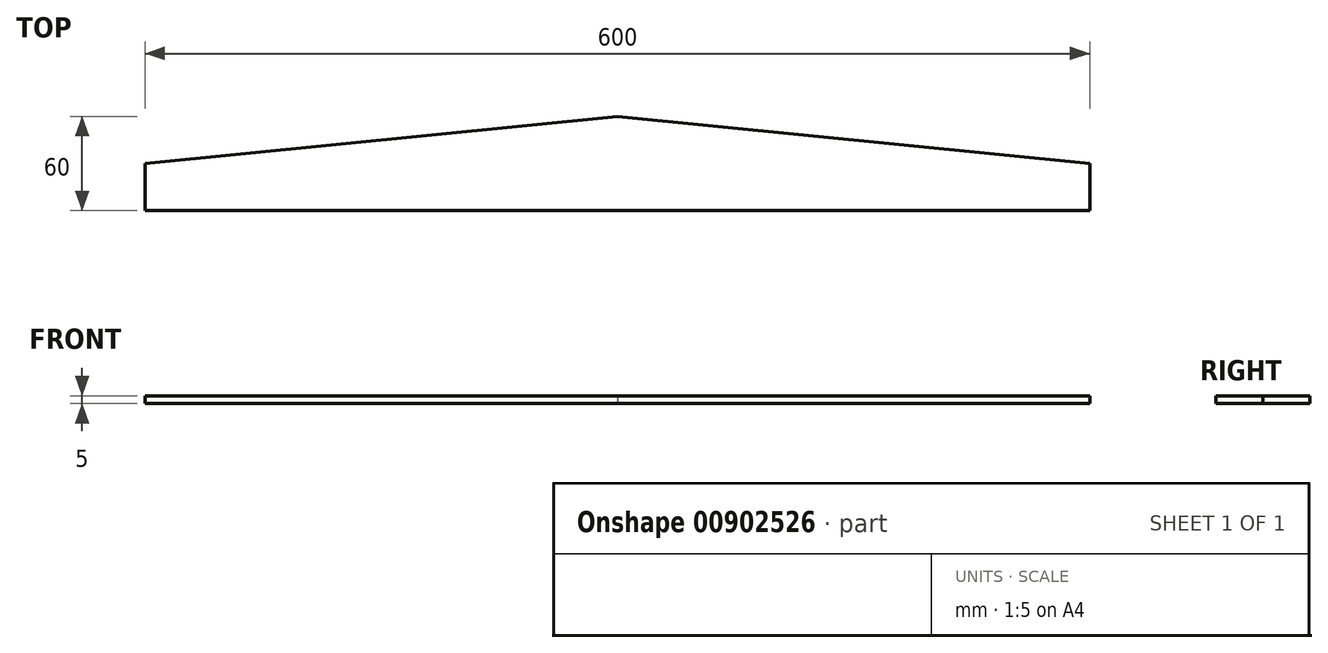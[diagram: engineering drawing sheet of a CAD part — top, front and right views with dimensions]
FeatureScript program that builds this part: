
annotation { "Feature Type Name" : "Feature", "Feature Type Description" : "" }
export const myFeature = defineFeature(function(context is Context, id is Id, definition is map)
    precondition{}
    {
        {
            var Q0;
            Q0=qCreatedBy(makeId("Top.planeOp"),FACE);
            var sketch = newSketch(context, id + "F0", { "sketchPlane" : qUnion([Q0])});
            skLineSegment(sketch, "E0", {"start": v(0, 0) * mm, "end": v(600, 0) * mm});
            skLineSegment(sketch, "E1", {"start": v(300, 0) * mm, "end": v(300, 60) * mm});
            skLineSegment(sketch, "E2", {"start": v(0, 0) * mm, "end": v(0, 30) * mm});
            skLineSegment(sketch, "E3", {"start": v(0, 30) * mm, "end": v(300, 60) * mm});
            skLineSegment(sketch, "E4", {"start": v(600, 0) * mm, "end": v(600, 30) * mm});
            skLineSegment(sketch, "E5", {"start": v(600, 30) * mm, "end": v(300, 60) * mm});
            skSolve(sketch);
        }
        {
            var Q0;
            {var subQ2=sQuery(id+"F0.wireOp",EDGE,"E1");Q0=makeQuery(id+"F0.imprint","IMPRINT",FACE,{"disambiguationData":[TD([[makeQuery(id+"F0.imprint","IMPRINT",EDGE,{"derivedFrom":subQ2}),1.0]])]});}
            var Q1;
            {var subQ2=sQuery(id+"F0.wireOp",EDGE,"E1");Q1=makeQuery(id+"F0.imprint","IMPRINT",FACE,{"disambiguationData":[TD([[makeQuery(id+"F0.imprint","IMPRINT",EDGE,{"derivedFrom":subQ2}),-1.0]])]});}
            extrude(context, id + "F1", {"entities" : qUnion([Q0, Q1]), "depth" : 5 * mm, "offsetDistance" : 25 * mm});
        }
    });
